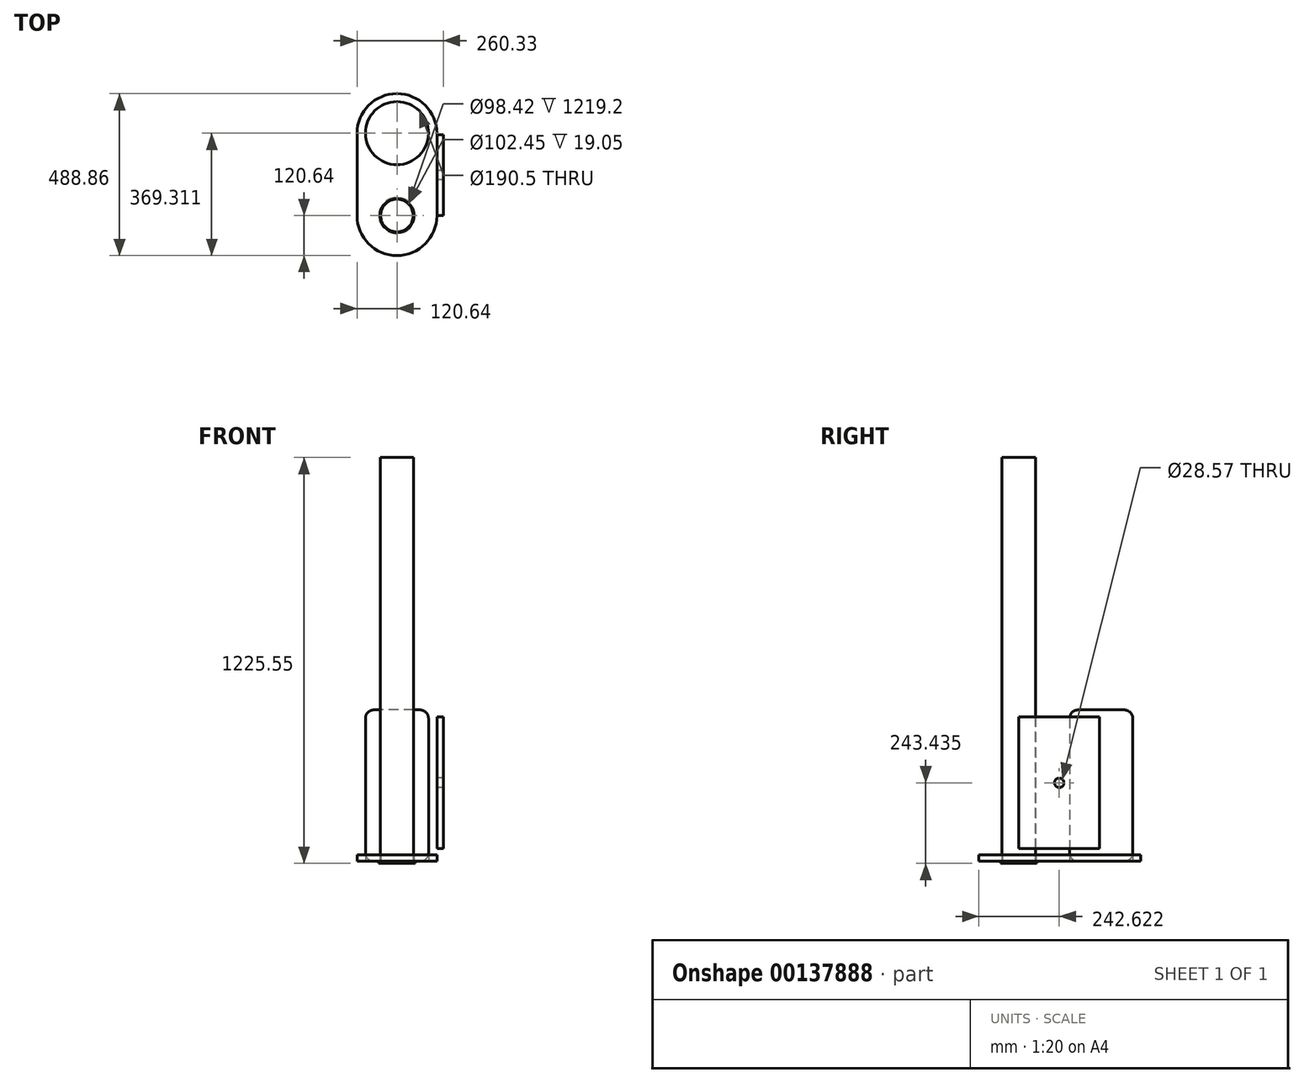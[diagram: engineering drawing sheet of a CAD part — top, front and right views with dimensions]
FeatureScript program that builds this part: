
annotation { "Feature Type Name" : "Feature", "Feature Type Description" : "" }
export const myFeature = defineFeature(function(context is Context, id is Id, definition is map)
    precondition{}
    {
        {
            var Q0;
            Q0=qCreatedBy(makeId("Top.planeOp"),FACE);
            var sketch = newSketch(context, id + "F0", { "sketchPlane" : qUnion([Q0])});
            skCircle(sketch, "E0", {"center": v(0, 0) * mm, "radius": 50.8 * mm});
            skCircle(sketch, "E1", {"center": v(0, 0) * mm, "radius": 49.21 * mm});
            skSolve(sketch);
        }
        {
            var Q0;
            Q0=makeQuery(id+"F0.imprint","IMPRINT",FACE,{"disambiguationData":[TD([[makeQuery(id+"F0.imprint","IMPRINT",EDGE,{"derivedFrom":sQuery(id+"F0.wireOp",EDGE,"E0")}),1.0]])]});
            extrude(context, id + "F1", {"entities" : qUnion([Q0]), "depth" : 1219.2 * mm});
        }
        {
            var Q0;
            Q0=qCreatedBy(makeId("Top.planeOp"),FACE);
            var sketch = newSketch(context, id + "F2", { "sketchPlane" : qUnion([Q0])});
            skCircle(sketch, "E2", {"center": v(0, 0) * mm, "radius": 51.22 * mm});
            skCircle(sketch, "E3", {"center": v(0, 0) * mm, "radius": 54.77 * mm});
            skSolve(sketch);
        }
        {
            var Q0;
            Q0=makeQuery(id+"F2.imprint","IMPRINT",FACE,{"disambiguationData":[TD([[makeQuery(id+"F2.imprint","IMPRINT",EDGE,{"derivedFrom":sQuery(id+"F2.wireOp",EDGE,"E2")}),-1.0]])]});
            extrude(context, id + "F3", {"entities" : qUnion([Q0]), "depth" : 12.33 * mm});
        }
        {
            var Q0;
            Q0=qCreatedBy(makeId("Top.planeOp"),FACE);
            var sketch = newSketch(context, id + "F4", { "sketchPlane" : qUnion([Q0])});
            skCircle(sketch, "E4", {"center": v(0, 0) * mm, "radius": 54.68 * mm});
            skSolve(sketch);
        }
        {
            var Q0;
            Q0 = qSketchRegion(id + "F4", true);
            extrude(context, id + "F5", {"entities" : qUnion([Q0]), "operationType" : NewBodyOperationType.ADD, "oppositeDirection" : true, "depth" : 6.35 * mm});
        }
        {
            var Q0;
            Q0=qCreatedBy(makeId("Top.planeOp"),FACE);
            var sketch = newSketch(context, id + "F6", { "sketchPlane" : qUnion([Q0])});
            skCircle(sketch, "E5", {"center": v(0, 248.67) * mm, "radius": 95.25 * mm});
            skSolve(sketch);
        }
        {
            var Q0;
            Q0 = qSketchRegion(id + "F6", true);
            extrude(context, id + "F7", {"entities" : qUnion([Q0]), "depth" : 457.2 * mm});
        }
        {
            var Q0;
            Q0=makeQuery(id+"F7.opExtrude","CAP_EDGE",EDGE,{"disambiguationData":[OSD([sQuery(id+"F6.wireOp",EDGE,"E5")])],"isStart":false});
            var Q1;
            Q1=makeQuery(id+"F7.opExtrude","CAP_EDGE",EDGE,{"disambiguationData":[OSD([sQuery(id+"F6.wireOp",EDGE,"E5")])],"isStart":true});
            fillet(context, id + "F8", {"entities" : qUnion([Q0, Q1]), "radius" : 25.4 * mm, "tangentPropagation" : true, "allowEdgeOverflow" : false});
        }
        {
            var Q0;
            Q0=qCreatedBy(makeId("Top.planeOp"),FACE);
            var sketch = newSketch(context, id + "F9", { "sketchPlane" : qUnion([Q0])});
            skLineSegment(sketch, "E6", {"start": v(120.64, 0) * mm, "end": v(120.64, 247.57) * mm});
            skLineSegment(sketch, "E7", {"start": v(0, 0) * mm, "end": v(0, 247.57) * mm, "construction": true});
            skLineSegment(sketch, "E8", {"start": v(0, 247.57) * mm, "end": v(125.96, 247.57) * mm, "construction": true});
            skArc(sketch, "E9", {"start": v(120.64, 247.57) * mm, "mid": v(0, 368.22) * mm, "end": v(-120.64, 247.57) * mm});
            skLineSegment(sketch, "E10", {"start": v(-120.64, 0) * mm, "end": v(-120.64, 247.57) * mm});
            skCircle(sketch, "E11.0", {"center": v(0, 248.67) * mm, "radius": 95.25 * mm});
            skCircle(sketch, "E12.0", {"center": v(0, 0) * mm, "radius": 51.22 * mm});
            skArc(sketch, "E13", {"start": v(120.64, 0) * mm, "mid": v(0, -120.64) * mm, "end": v(-120.64, 0) * mm});
            skSolve(sketch);
        }
        {
            var Q0;
            Q0=makeQuery(id+"F9.imprint","IMPRINT",FACE,{"disambiguationData":[TD([[makeQuery(id+"F9.imprint","IMPRINT",EDGE,{"derivedFrom":sQuery(id+"F9.wireOp",EDGE,"E6")}),1.0]])]});
            extrude(context, id + "F10", {"entities" : qUnion([Q0]), "operationType" : NewBodyOperationType.ADD, "depth" : 19.05 * mm});
        }
        {
            var Q0;
            Q0=makeQuery(id+"F10.opExtrude","SWEPT_FACE",FACE,{"disambiguationData":[OSD([sQuery(id+"F9.wireOp",EDGE,"E6")])]});
            var sketch = newSketch(context, id + "F11", { "sketchPlane" : qUnion([Q0])});
            skLineSegment(sketch, "E14.bottom", {"start": v(0, 38.7) * mm, "end": v(243.96, 38.7) * mm});
            skLineSegment(sketch, "E14.top", {"start": v(0, 435.47) * mm, "end": v(243.96, 435.47) * mm});
            skLineSegment(sketch, "E14.left", {"start": v(0, 38.7) * mm, "end": v(0, 435.47) * mm});
            skLineSegment(sketch, "E14.right", {"start": v(243.96, 38.7) * mm, "end": v(243.96, 435.47) * mm});
            skCircle(sketch, "E15", {"center": v(121.98, 237.08) * mm, "radius": 14.29 * mm});
            skPoint(sketch, "E15.centerSnap0", {"position": v(121.98, 38.7) * mm});
            skPoint(sketch, "E15.centerSnap1", {"position": v(0, 237.08) * mm});
            skSolve(sketch);
        }
        {
            var Q0;
            Q0=makeQuery(id+"F11.imprint","IMPRINT",FACE,{"disambiguationData":[TD([[makeQuery(id+"F11.imprint","IMPRINT",EDGE,{"derivedFrom":sQuery(id+"F11.wireOp",EDGE,"E14.bottom")}),1.0]])]});
            extrude(context, id + "F12", {"entities" : qUnion([Q0]), "depth" : 19.05 * mm});
        }
    });
